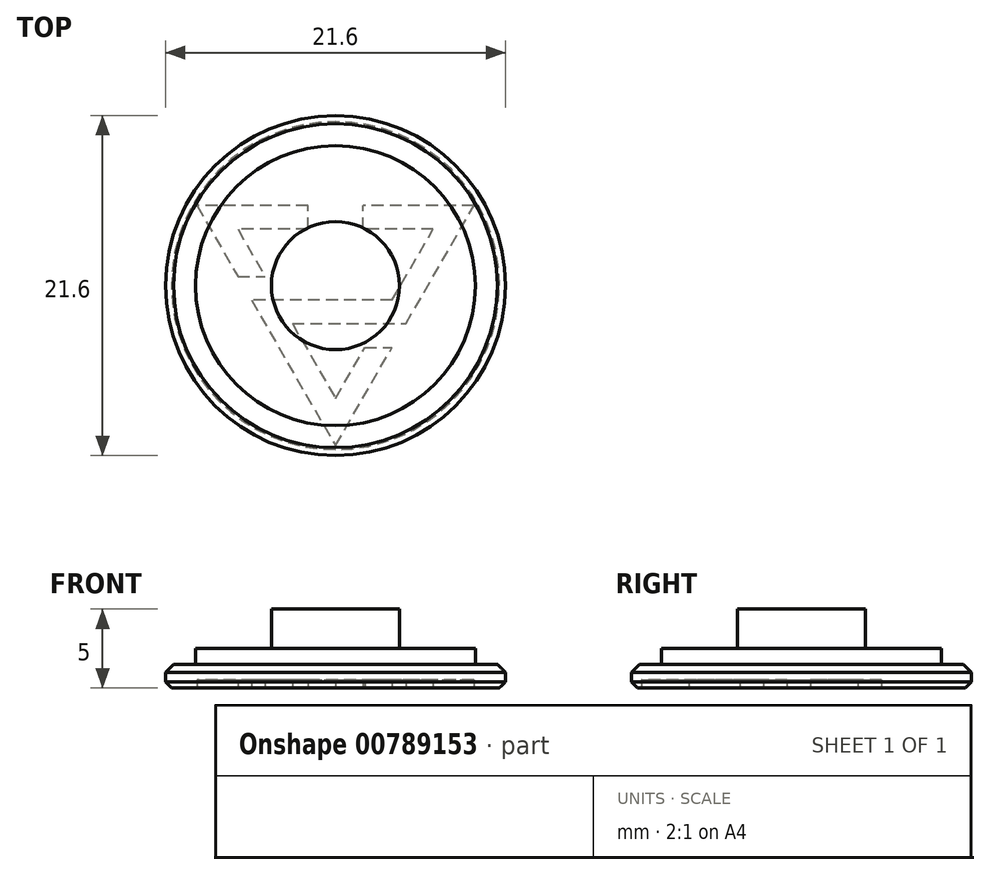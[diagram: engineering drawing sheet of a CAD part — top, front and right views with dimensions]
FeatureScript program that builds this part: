
annotation { "Feature Type Name" : "Feature", "Feature Type Description" : "" }
export const myFeature = defineFeature(function(context is Context, id is Id, definition is map)
    precondition{}
    {
        {
            var Q0;
            Q0=qCreatedBy(makeId("Top.planeOp"),FACE);
            var sketch = newSketch(context, id + "F0", { "sketchPlane" : qUnion([Q0])});
            skCircle(sketch, "E0", {"center": v(0, 0) * mm, "radius": 10.8 * mm});
            skCircle(sketch, "E1", {"center": v(0, 0) * mm, "radius": 8.9 * mm});
            skCircle(sketch, "E2", {"center": v(0, 0) * mm, "radius": 4.06 * mm});
            skSolve(sketch);
        }
        {
            var Q0;
            Q0=makeQuery(id+"F0.imprint","IMPRINT",FACE,{"disambiguationData":[TD([[makeQuery(id+"F0.imprint","IMPRINT",EDGE,{"derivedFrom":sQuery(id+"F0.wireOp",EDGE,"E2")}),1.0]])]});
            extrude(context, id + "F1", {"entities" : qUnion([Q0]), "depth" : 5 * mm, "offsetDistance" : 25.4 * mm});
        }
        {
            var Q0;
            Q0=makeQuery(id+"F0.imprint","IMPRINT",FACE,{"disambiguationData":[TD([[makeQuery(id+"F0.imprint","IMPRINT",EDGE,{"derivedFrom":sQuery(id+"F0.wireOp",EDGE,"E1")}),1.0]])]});
            extrude(context, id + "F2", {"entities" : qUnion([Q0]), "operationType" : NewBodyOperationType.ADD, "depth" : 2.5 * mm, "offsetDistance" : 25.4 * mm});
        }
        {
            var Q0;
            Q0=makeQuery(id+"F0.imprint","IMPRINT",FACE,{"disambiguationData":[TD([[makeQuery(id+"F0.imprint","IMPRINT",EDGE,{"derivedFrom":sQuery(id+"F0.wireOp",EDGE,"E0")}),1.0]])]});
            extrude(context, id + "F3", {"entities" : qUnion([Q0]), "operationType" : NewBodyOperationType.ADD, "depth" : 1.5 * mm, "offsetDistance" : 25.4 * mm});
        }
        {
            var Q0;
            {var subQ0=sQuery(id+"F0.wireOp",EDGE,"E1");var subQ1=sQuery(id+"F0.wireOp",EDGE,"E2");Q0=makeQuery(id+"F3.boolean.opBoolean","MERGE",FACE,{"derivedFrom":[makeQuery(id+"F2.boolean.opBoolean","MERGE",FACE,{"derivedFrom":[makeQuery(id+"F1.opExtrude","CAP_FACE",FACE,{"disambiguationData":[OSD([subQ1])],"isStart":true}),makeQuery(id+"F2.opExtrude","CAP_FACE",FACE,{"disambiguationData":[OSD([subQ0,subQ1])],"isStart":true})]}),makeQuery(id+"F3.opExtrude","CAP_FACE",FACE,{"disambiguationData":[OSD([sQuery(id+"F0.wireOp",EDGE,"E0"),subQ0])],"isStart":true})]});}
            var sketch = newSketch(context, id + "F4", { "sketchPlane" : qUnion([Q0])});
            skCircle(sketch, "E3.cCircle", {"center": v(0, 0) * mm, "radius": 10.16 * mm, "construction": true});
            skLineSegment(sketch, "E3.0", {"start": v(-8.8, -5.08) * mm, "end": v(0, 10.16) * mm});
            skLineSegment(sketch, "E3.1", {"start": v(0, 10.16) * mm, "end": v(8.8, -5.08) * mm});
            skLineSegment(sketch, "E3.2", {"start": v(8.8, -5.08) * mm, "end": v(-8.8, -5.08) * mm});
            skCircle(sketch, "E4.cCircle", {"center": v(0, 0) * mm, "radius": 7.16 * mm, "construction": true});
            skLineSegment(sketch, "E4.0", {"start": v(-6.2, -3.58) * mm, "end": v(0, 7.16) * mm});
            skLineSegment(sketch, "E4.1", {"start": v(0, 7.16) * mm, "end": v(6.2, -3.58) * mm});
            skLineSegment(sketch, "E4.2", {"start": v(6.2, -3.58) * mm, "end": v(-6.2, -3.58) * mm});
            skLineSegment(sketch, "E5", {"start": v(-3.6, 0.92) * mm, "end": v(3.6, 0.92) * mm});
            skLineSegment(sketch, "E6", {"start": v(2.74, 2.42) * mm, "end": v(-2.74, 2.42) * mm});
            skLineSegment(sketch, "E7", {"start": v(1.87, 3.92) * mm, "end": v(3.6, 3.92) * mm});
            skLineSegment(sketch, "E8", {"start": v(-6.2, -0.58) * mm, "end": v(-4.47, -0.58) * mm});
            skLineSegment(sketch, "E9", {"start": v(-1.75, -3.58) * mm, "end": v(-1.75, -5.08) * mm});
            skLineSegment(sketch, "E10", {"start": v(1.75, -3.58) * mm, "end": v(1.75, -5.08) * mm});
            skLineSegment(sketch, "E11", {"start": v(0, 10.16) * mm, "end": v(0, -5.08) * mm, "construction": true});
            skLineSegment(sketch, "E12", {"start": v(-3.6, 0.92) * mm, "end": v(-5.33, 0.92) * mm});
            skLineSegment(sketch, "E13", {"start": v(2.74, 2.42) * mm, "end": v(4.47, 2.42) * mm});
            skSolve(sketch);
        }
        {
            var Q0;
            {var subQ7=sQuery(id+"F4.wireOp",EDGE,"E8");Q0=makeQuery(id+"F4.imprint","IMPRINT",FACE,{"disambiguationData":[TD([[makeQuery(id+"F4.imprint","IMPRINT",EDGE,{"derivedFrom":subQ7}),-1.0]])]});}
            var Q1;
            {var subQ3=sQuery(id+"F4.wireOp",EDGE,"E7");Q1=makeQuery(id+"F4.imprint","IMPRINT",FACE,{"disambiguationData":[TD([[makeQuery(id+"F4.imprint","IMPRINT",EDGE,{"derivedFrom":subQ3}),1.0]])]});}
            var Q2;
            {var subQ8=sQuery(id+"F4.wireOp",EDGE,"E10");Q2=makeQuery(id+"F4.imprint","IMPRINT",FACE,{"disambiguationData":[TD([[makeQuery(id+"F4.imprint","IMPRINT",EDGE,{"derivedFrom":subQ8}),1.0]])]});}
            var Q3;
            {var subQ0=sQuery(id+"F4.wireOp",EDGE,"E5");Q3=makeQuery(id+"F4.imprint","IMPRINT",FACE,{"disambiguationData":[TD([[makeQuery(id+"F4.imprint","IMPRINT",EDGE,{"derivedFrom":subQ0}),1.0]])]});}
            extrude(context, id + "F5", {"entities" : qUnion([Q0, Q1, Q2, Q3]), "operationType" : NewBodyOperationType.REMOVE, "oppositeDirection" : true, "depth" : .5 * mm, "offsetDistance" : 25.4 * mm});
        }
        {
            var Q0;
            Q0=makeQuery(id+"F3.opExtrude","CAP_EDGE",EDGE,{"disambiguationData":[OSD([sQuery(id+"F0.wireOp",EDGE,"E0")])],"isStart":false});
            chamfer(context, id + "F6", {"entities" : qUnion([Q0]), "width" : 0.5 * mm});
        }
        {
            var Q0;
            Q0=makeQuery(id+"F3.opExtrude","CAP_EDGE",EDGE,{"disambiguationData":[OSD([sQuery(id+"F0.wireOp",EDGE,"E0")])],"isStart":true});
            chamfer(context, id + "F7", {"entities" : qUnion([Q0]), "width" : 0.38 * mm, "tangentPropagation" : true});
        }
    });
